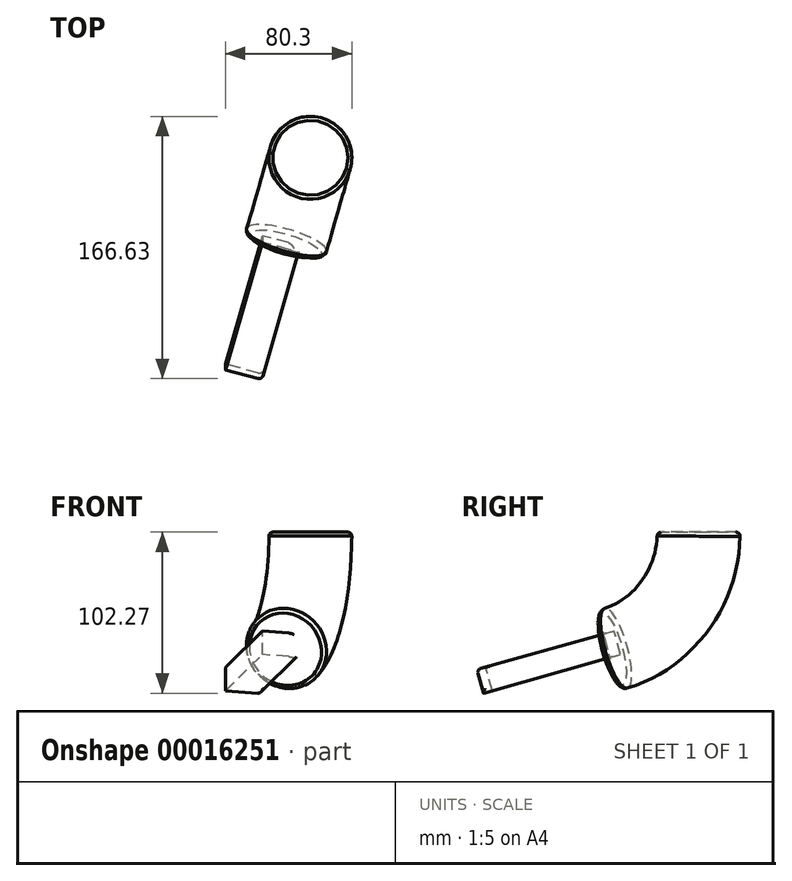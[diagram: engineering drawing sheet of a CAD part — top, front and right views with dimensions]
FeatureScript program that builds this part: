
annotation { "Feature Type Name" : "Feature", "Feature Type Description" : "" }
export const myFeature = defineFeature(function(context is Context, id is Id, definition is map)
    precondition{}
    {
        {
            var Q0;
            Q0=qCreatedBy(makeId("Top.planeOp"),FACE);
            var sketch = newSketch(context, id + "F3", { "sketchPlane" : qUnion([Q0])});
            skLineSegment(sketch, "E0", {"start": v(-53.5, -40.28) * mm, "end": v(0, -55.72) * mm});
            skCircle(sketch, "E1", {"center": v(24.76, 17.4) * mm, "radius": 26.32 * mm});
            skSolve(sketch);
        }
        {
            var Q0;
            Q0 = qSketchRegion(id + "F3", true);
            var Q1;
            Q1=sQuery(id+"F3.wireOp",EDGE,"E0");
            revolve(context, id + "F0", {"entities" : qUnion([Q0]), "axis" : qUnion([Q1]), "revolveType" : RevolveType.ONE_DIRECTION, "oppositeDirection" : true, "angle" : 74.87 * degree});
        }
        {
            var Q0;
            Q0=makeQuery(id+"F0.opRevolve","CAP_FACE",FACE,{"disambiguationData":[OSD([sQuery(id+"F3.wireOp",EDGE,"E1")])],"isStart":false});
            var sketch = newSketch(context, id + "F1", { "sketchPlane" : qUnion([Q0])});
            skLineSegment(sketch, "E2.bottom", {"start": v(32.48, -66.14) * mm, "end": v(8.44, -66.14) * mm});
            skLineSegment(sketch, "E2.top", {"start": v(32.48, -50.65) * mm, "end": v(8.44, -50.65) * mm});
            skLineSegment(sketch, "E2.left", {"start": v(32.48, -66.14) * mm, "end": v(32.48, -50.65) * mm});
            skLineSegment(sketch, "E2.right", {"start": v(8.44, -66.14) * mm, "end": v(8.44, -50.65) * mm});
            skSolve(sketch);
        }
        {
            var Q0;
            Q0 = qSketchRegion(id + "F1", true);
            var Q1;
            Q1=makeQuery(id+"F1.imprint","IMPRINT",FACE,{"disambiguationData":[TD([[makeQuery(id+"F1.imprint","IMPRINT",EDGE,{"derivedFrom":sQuery(id+"F1.wireOp",EDGE,"E2.bottom")}),-1.0]])]});
            extrude(context, id + "F4", {"entities" : qUnion([Q0, Q1]), "operationType" : NewBodyOperationType.ADD, "depth" : 87.9 * mm});
        }
        {
            var Q0;
            Q0=makeQuery(id+"F0.opRevolve","CAP_FACE",FACE,{"disambiguationData":[OSD([sQuery(id+"F3.wireOp",EDGE,"E1")])],"isStart":true});
            var Q1;
            Q1=makeQuery(id+"F0.opRevolve","CAP_EDGE",EDGE,{"disambiguationData":[OSD([sQuery(id+"F3.wireOp",EDGE,"E1")])],"isStart":false});
            var Q2;
            Q2=makeQuery(id+"F4.opExtrude","CAP_EDGE",EDGE,{"disambiguationData":[OSD([sQuery(id+"F1.wireOp",EDGE,"E2.top")])],"isStart":false});
            var Q3;
            Q3=makeQuery(id+"F4.opExtrude","SWEPT_FACE",FACE,{"disambiguationData":[OSD([sQuery(id+"F1.wireOp",EDGE,"E2.left")])]});
            fillet(context, id + "F2", {"entities" : qUnion([Q0, Q1, Q2, Q3]), "radius" : 2.54 * mm, "tangentPropagation" : true, "allowEdgeOverflow" : false});
        }
    });
